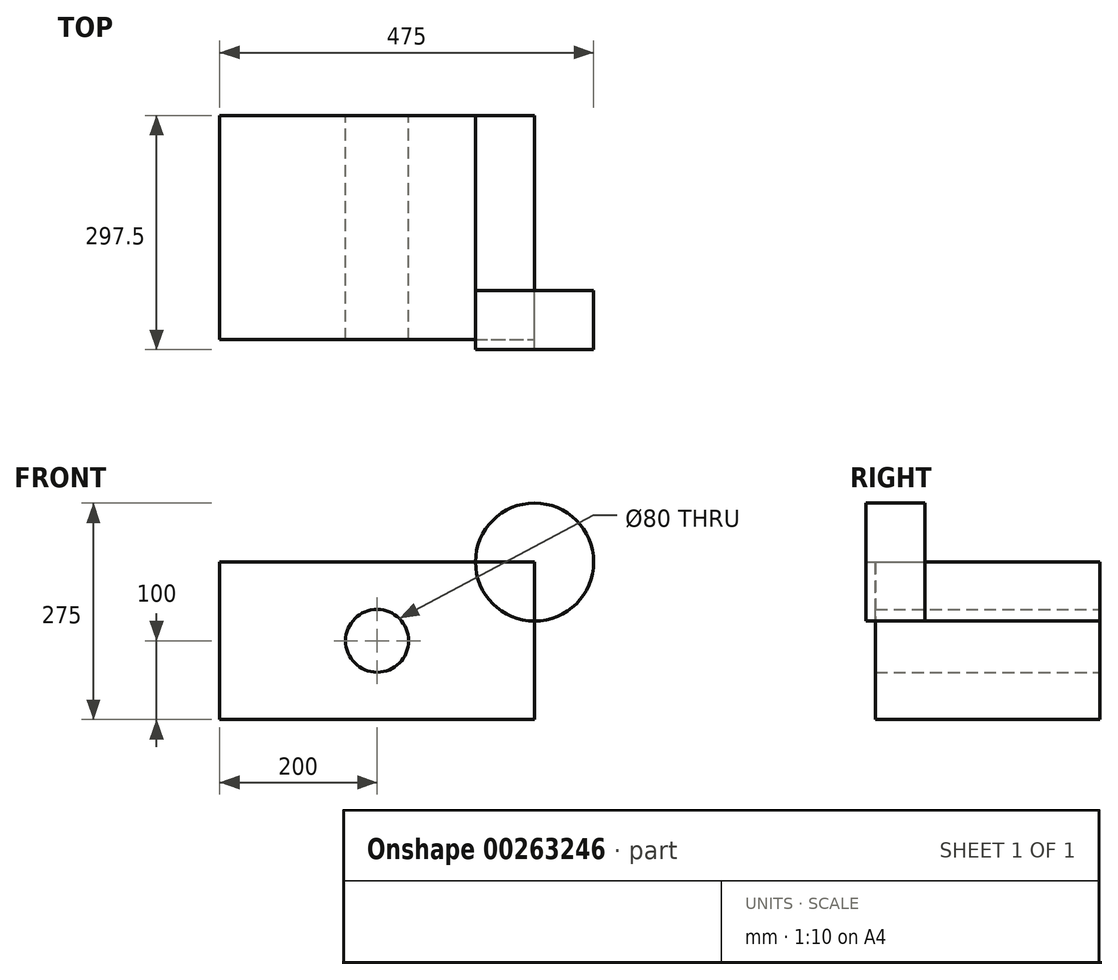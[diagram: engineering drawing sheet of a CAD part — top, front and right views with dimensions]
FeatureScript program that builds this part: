
annotation { "Feature Type Name" : "Feature", "Feature Type Description" : "" }
export const myFeature = defineFeature(function(context is Context, id is Id, definition is map)
    precondition{}
    {
        {
            var Q0;
            Q0=qCreatedBy(makeId("Front.planeOp"),FACE);
            var sketch = newSketch(context, id + "F0", { "sketchPlane" : qUnion([Q0])});
            skLineSegment(sketch, "E0.bottom", {"start": v(-200, -100) * mm, "end": v(200, -100) * mm});
            skLineSegment(sketch, "E0.top", {"start": v(-200, 100) * mm, "end": v(200, 100) * mm});
            skLineSegment(sketch, "E0.left", {"start": v(-200, -100) * mm, "end": v(-200, 100) * mm});
            skLineSegment(sketch, "E0.right", {"start": v(200, -100) * mm, "end": v(200, 100) * mm});
            skPoint(sketch, "E0.middle", {"position": v(0, 0) * mm});
            skCircle(sketch, "E1", {"center": v(200, 100) * mm, "radius": 75 * mm});
            skArc(sketch, "E2", {"start": v(202.24, 174.97) * mm, "mid": v(-13.64, 216.7) * mm, "end": v(-200, 100) * mm});
            skCircle(sketch, "E3", {"center": v(0, 0) * mm, "radius": 40 * mm});
            skSolve(sketch);
        }
        {
            var Q0;
            {var subQ1=sQuery(id+"F0.wireOp",EDGE,"E0.bottom");Q0=makeQuery(id+"F0.imprint","IMPRINT",FACE,{"disambiguationData":[TD([[makeQuery(id+"F0.imprint","IMPRINT",EDGE,{"derivedFrom":subQ1}),1.0]])]});}
            extrude(context, id + "F1", {"entities" : qUnion([Q0]), "depth" : 50 * mm, "symmetric" : true});
        }
        {
            var Q0;
            Q0=makeQuery(id+"F1.opExtrude","CAP_FACE",FACE,{"disambiguationData":[OSD([sQuery(id+"F0.wireOp",EDGE,"E0.bottom"),sQuery(id+"F0.wireOp",EDGE,"E0.top"),sQuery(id+"F0.wireOp",EDGE,"E0.left"),sQuery(id+"F0.wireOp",EDGE,"E0.right"),sQuery(id+"F0.wireOp",EDGE,"E1")])],"isStart":false});
            extrude(context, id + "F2", {"entities" : qUnion([Q0]), "operationType" : NewBodyOperationType.ADD, "oppositeDirection" : true, "depth" : 285 * mm});
        }
        {
            var Q0;
            {var subQ0=sQuery(id+"F0.wireOp",EDGE,"E0.right");var subQ1=sQuery(id+"F0.wireOp",EDGE,"E0.top");var subQ2=makeQuery(id+"F0.imprint","INTERSECT",VERTEX,{"derivedFrom":[subQ1,subQ0]});Q0=makeQuery(id+"F0.imprint","IMPRINT",FACE,{"disambiguationData":[TD([[makeQuery(id+"F0.imprint","IMPRINT",EDGE,{"disambiguationData":[TD([[subQ2,1.0]])],"derivedFrom":subQ0}),-1.0]])]});}
            extrude(context, id + "F3", {"entities" : qUnion([Q0]), "depth" : 75 * mm, "symmetric" : true});
        }
    });
